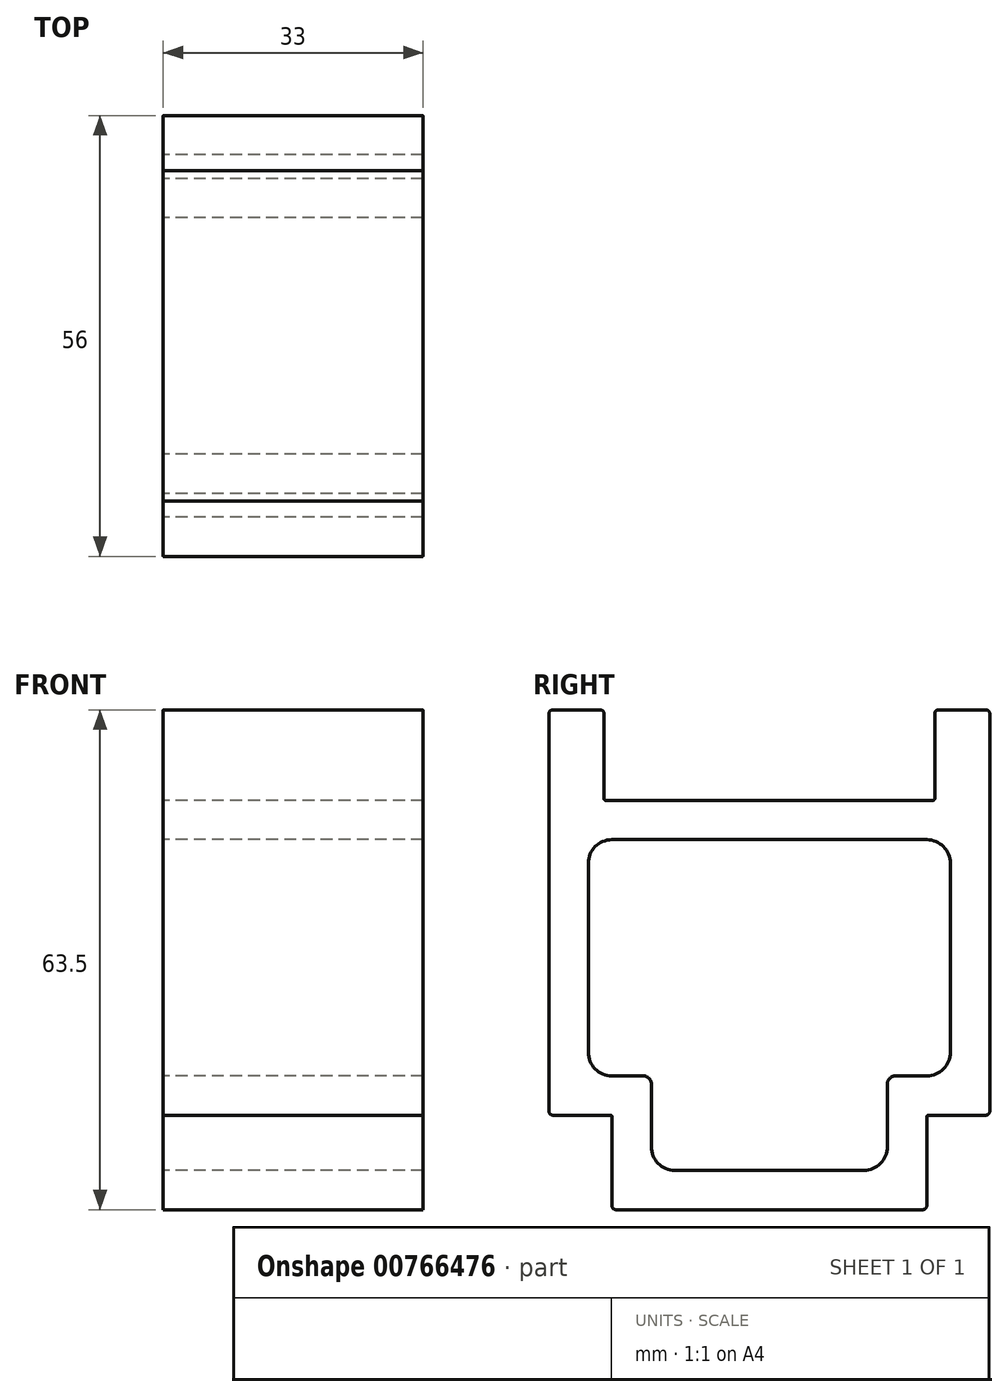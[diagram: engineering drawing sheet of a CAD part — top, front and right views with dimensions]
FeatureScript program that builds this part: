
annotation { "Feature Type Name" : "Feature", "Feature Type Description" : "" }
export const myFeature = defineFeature(function(context is Context, id is Id, definition is map)
    precondition{}
    {
        {
            var Q0;
            Q0=qCreatedBy(makeId("Right.planeOp"),FACE);
            var sketch = newSketch(context, id + "F0", { "sketchPlane" : qUnion([Q0])});
            skLineSegment(sketch, "E0", {"start": v(-20, 0) * mm, "end": v(-20, 12) * mm});
            skLineSegment(sketch, "E1", {"start": v(-20, 12) * mm, "end": v(-28, 12) * mm});
            skLineSegment(sketch, "E2", {"start": v(-28, 12) * mm, "end": v(-28, 63.5) * mm});
            skLineSegment(sketch, "E3", {"start": v(-28, 63.5) * mm, "end": v(-21, 63.5) * mm});
            skLineSegment(sketch, "E4", {"start": v(-21, 63.5) * mm, "end": v(-21, 52) * mm});
            skLineSegment(sketch, "E5.MirrorCS", {"start": v(21, 63.5) * mm, "end": v(21, 52) * mm});
            skLineSegment(sketch, "E6.MirrorCS", {"start": v(28, 63.5) * mm, "end": v(21, 63.5) * mm});
            skLineSegment(sketch, "E7.MirrorCS", {"start": v(28, 12) * mm, "end": v(28, 63.5) * mm});
            skLineSegment(sketch, "E8.MirrorCS", {"start": v(20, 12) * mm, "end": v(28, 12) * mm});
            skLineSegment(sketch, "E9.MirrorCS", {"start": v(20, 0) * mm, "end": v(20, 12) * mm});
            skLineSegment(sketch, "E10", {"start": v(-21, 52) * mm, "end": v(21, 52) * mm});
            skLineSegment(sketch, "E11", {"start": v(-20, 0) * mm, "end": v(20, 0) * mm});
            skSolve(sketch);
        }
        {
            var Q0;
            Q0=makeQuery(id+"F0.imprint","IMPRINT",FACE,{"disambiguationData":[TD([[makeQuery(id+"F0.imprint","IMPRINT",EDGE,{"derivedFrom":sQuery(id+"F0.wireOp",EDGE,"E0")}),-1.0]])]});
            extrude(context, id + "F1", {"entities" : qUnion([Q0]), "depth" : 33 * mm, "offsetDistance" : 25 * mm});
        }
        {
            var Q0;
            Q0=makeQuery(id+"F1.opExtrude","CAP_FACE",FACE,{"disambiguationData":[OSD([sQuery(id+"F0.wireOp",EDGE,"E0"),sQuery(id+"F0.wireOp",EDGE,"E1"),sQuery(id+"F0.wireOp",EDGE,"E2"),sQuery(id+"F0.wireOp",EDGE,"E3"),sQuery(id+"F0.wireOp",EDGE,"E4"),sQuery(id+"F0.wireOp",EDGE,"E5.MirrorCS"),sQuery(id+"F0.wireOp",EDGE,"E6.MirrorCS"),sQuery(id+"F0.wireOp",EDGE,"E7.MirrorCS"),sQuery(id+"F0.wireOp",EDGE,"E8.MirrorCS"),sQuery(id+"F0.wireOp",EDGE,"E9.MirrorCS"),sQuery(id+"F0.wireOp",EDGE,"E10"),sQuery(id+"F0.wireOp",EDGE,"E11")])],"isStart":false});
            var Q1;
            Q1=makeQuery(id+"F1.opExtrude","CAP_FACE",FACE,{"disambiguationData":[OSD([sQuery(id+"F0.wireOp",EDGE,"E0"),sQuery(id+"F0.wireOp",EDGE,"E1"),sQuery(id+"F0.wireOp",EDGE,"E2"),sQuery(id+"F0.wireOp",EDGE,"E3"),sQuery(id+"F0.wireOp",EDGE,"E4"),sQuery(id+"F0.wireOp",EDGE,"E5.MirrorCS"),sQuery(id+"F0.wireOp",EDGE,"E6.MirrorCS"),sQuery(id+"F0.wireOp",EDGE,"E7.MirrorCS"),sQuery(id+"F0.wireOp",EDGE,"E8.MirrorCS"),sQuery(id+"F0.wireOp",EDGE,"E9.MirrorCS"),sQuery(id+"F0.wireOp",EDGE,"E10"),sQuery(id+"F0.wireOp",EDGE,"E11")])],"isStart":true});
            shell(context, id + "F2", {"entities" : qUnion([Q0, Q1]), "thickness" : 5 * mm});
        }
        {
            var Q0;
            Q0=makeQuery(id+"F1.opExtrude","SWEPT_EDGE",EDGE,{"disambiguationData":[OSD([sQuery(id+"F0.wireOp",EDGE,"E8.MirrorCS"),sQuery(id+"F0.wireOp",EDGE,"E9.MirrorCS")])]});
            var Q1;
            Q1=makeQuery(id+"F1.opExtrude","SWEPT_EDGE",EDGE,{"disambiguationData":[OSD([sQuery(id+"F0.wireOp",EDGE,"E0"),sQuery(id+"F0.wireOp",EDGE,"E1")])]});
            var Q2;
            Q2=makeQuery(id+"F1.opExtrude","SWEPT_EDGE",EDGE,{"disambiguationData":[OSD([sQuery(id+"F0.wireOp",EDGE,"E4"),sQuery(id+"F0.wireOp",EDGE,"E10")])]});
            var Q3;
            Q3=makeQuery(id+"F1.opExtrude","SWEPT_EDGE",EDGE,{"disambiguationData":[OSD([sQuery(id+"F0.wireOp",EDGE,"E5.MirrorCS"),sQuery(id+"F0.wireOp",EDGE,"E10")])]});
            fillet(context, id + "F3", {"entities" : qUnion([Q0, Q1, Q2, Q3]), "radius" : 0.2 * mm, "tangentPropagation" : true, "allowEdgeOverflow" : false});
        }
        {
            var Q0;
            Q0=makeQuery(id+"F1.opExtrude","SWEPT_EDGE",EDGE,{"disambiguationData":[OSD([sQuery(id+"F0.wireOp",EDGE,"E5.MirrorCS"),sQuery(id+"F0.wireOp",EDGE,"E6.MirrorCS")])]});
            var Q1;
            Q1=makeQuery(id+"F1.opExtrude","SWEPT_EDGE",EDGE,{"disambiguationData":[OSD([sQuery(id+"F0.wireOp",EDGE,"E6.MirrorCS"),sQuery(id+"F0.wireOp",EDGE,"E7.MirrorCS")])]});
            var Q2;
            Q2=makeQuery(id+"F1.opExtrude","SWEPT_EDGE",EDGE,{"disambiguationData":[OSD([sQuery(id+"F0.wireOp",EDGE,"E7.MirrorCS"),sQuery(id+"F0.wireOp",EDGE,"E8.MirrorCS")])]});
            var Q3;
            Q3=makeQuery(id+"F1.opExtrude","SWEPT_EDGE",EDGE,{"disambiguationData":[OSD([sQuery(id+"F0.wireOp",EDGE,"E9.MirrorCS"),sQuery(id+"F0.wireOp",EDGE,"E11")])]});
            var Q4;
            Q4=makeQuery(id+"F1.opExtrude","SWEPT_EDGE",EDGE,{"disambiguationData":[OSD([sQuery(id+"F0.wireOp",EDGE,"E0"),sQuery(id+"F0.wireOp",EDGE,"E11")])]});
            var Q5;
            Q5=makeQuery(id+"F1.opExtrude","SWEPT_EDGE",EDGE,{"disambiguationData":[OSD([sQuery(id+"F0.wireOp",EDGE,"E1"),sQuery(id+"F0.wireOp",EDGE,"E2")])]});
            var Q6;
            Q6=makeQuery(id+"F1.opExtrude","SWEPT_EDGE",EDGE,{"disambiguationData":[OSD([sQuery(id+"F0.wireOp",EDGE,"E2"),sQuery(id+"F0.wireOp",EDGE,"E3")])]});
            var Q7;
            Q7=makeQuery(id+"F1.opExtrude","SWEPT_EDGE",EDGE,{"disambiguationData":[OSD([sQuery(id+"F0.wireOp",EDGE,"E3"),sQuery(id+"F0.wireOp",EDGE,"E4")])]});
            fillet(context, id + "F4", {"entities" : qUnion([Q0, Q1, Q2, Q3, Q4, Q5, Q6, Q7]), "radius" : .5 * mm, "tangentPropagation" : true, "allowEdgeOverflow" : false});
        }
        {
            var Q0;
            Q0=makeQuery(id+"F2.opShell","TWEAK_EDGE",EDGE,{"derivedFrom":[makeQuery(id+"F1.opExtrude","SWEPT_FACE",FACE,{"disambiguationData":[OSD([sQuery(id+"F0.wireOp",EDGE,"E7.MirrorCS")])]}),makeQuery(id+"F1.opExtrude","SWEPT_FACE",FACE,{"disambiguationData":[OSD([sQuery(id+"F0.wireOp",EDGE,"E10")])]})]});
            var Q1;
            Q1=makeQuery(id+"F2.opShell","TWEAK_EDGE",EDGE,{"derivedFrom":[makeQuery(id+"F1.opExtrude","SWEPT_FACE",FACE,{"disambiguationData":[OSD([sQuery(id+"F0.wireOp",EDGE,"E2")])]}),makeQuery(id+"F1.opExtrude","SWEPT_FACE",FACE,{"disambiguationData":[OSD([sQuery(id+"F0.wireOp",EDGE,"E10")])]})]});
            var Q2;
            Q2=makeQuery(id+"F2.opShell","OFFSET_EDGE",EDGE,{"disambiguationData":[OSD([sQuery(id+"F0.wireOp",EDGE,"E1"),sQuery(id+"F0.wireOp",EDGE,"E2")])]});
            var Q3;
            Q3=makeQuery(id+"F2.opShell","OFFSET_EDGE",EDGE,{"disambiguationData":[OSD([sQuery(id+"F0.wireOp",EDGE,"E7.MirrorCS"),sQuery(id+"F0.wireOp",EDGE,"E8.MirrorCS")])]});
            var Q4;
            Q4=makeQuery(id+"F2.opShell","OFFSET_EDGE",EDGE,{"disambiguationData":[OSD([sQuery(id+"F0.wireOp",EDGE,"E9.MirrorCS"),sQuery(id+"F0.wireOp",EDGE,"E11")])]});
            var Q5;
            Q5=makeQuery(id+"F2.opShell","OFFSET_EDGE",EDGE,{"disambiguationData":[OSD([sQuery(id+"F0.wireOp",EDGE,"E0"),sQuery(id+"F0.wireOp",EDGE,"E11")])]});
            fillet(context, id + "F5", {"entities" : qUnion([Q0, Q1, Q2, Q3, Q4, Q5]), "radius" : 3 * mm, "tangentPropagation" : true, "allowEdgeOverflow" : false});
        }
        {
            var Q0;
            Q0=makeQuery(id+"F2.opShell","OFFSET_EDGE",EDGE,{"disambiguationData":[OSD([sQuery(id+"F0.wireOp",EDGE,"E0"),sQuery(id+"F0.wireOp",EDGE,"E1")])]});
            var Q1;
            Q1=makeQuery(id+"F2.opShell","OFFSET_EDGE",EDGE,{"disambiguationData":[OSD([sQuery(id+"F0.wireOp",EDGE,"E8.MirrorCS"),sQuery(id+"F0.wireOp",EDGE,"E9.MirrorCS")])]});
            fillet(context, id + "F6", {"entities" : qUnion([Q0, Q1]), "radius" : 1 * mm, "tangentPropagation" : true, "allowEdgeOverflow" : false});
        }
    });
